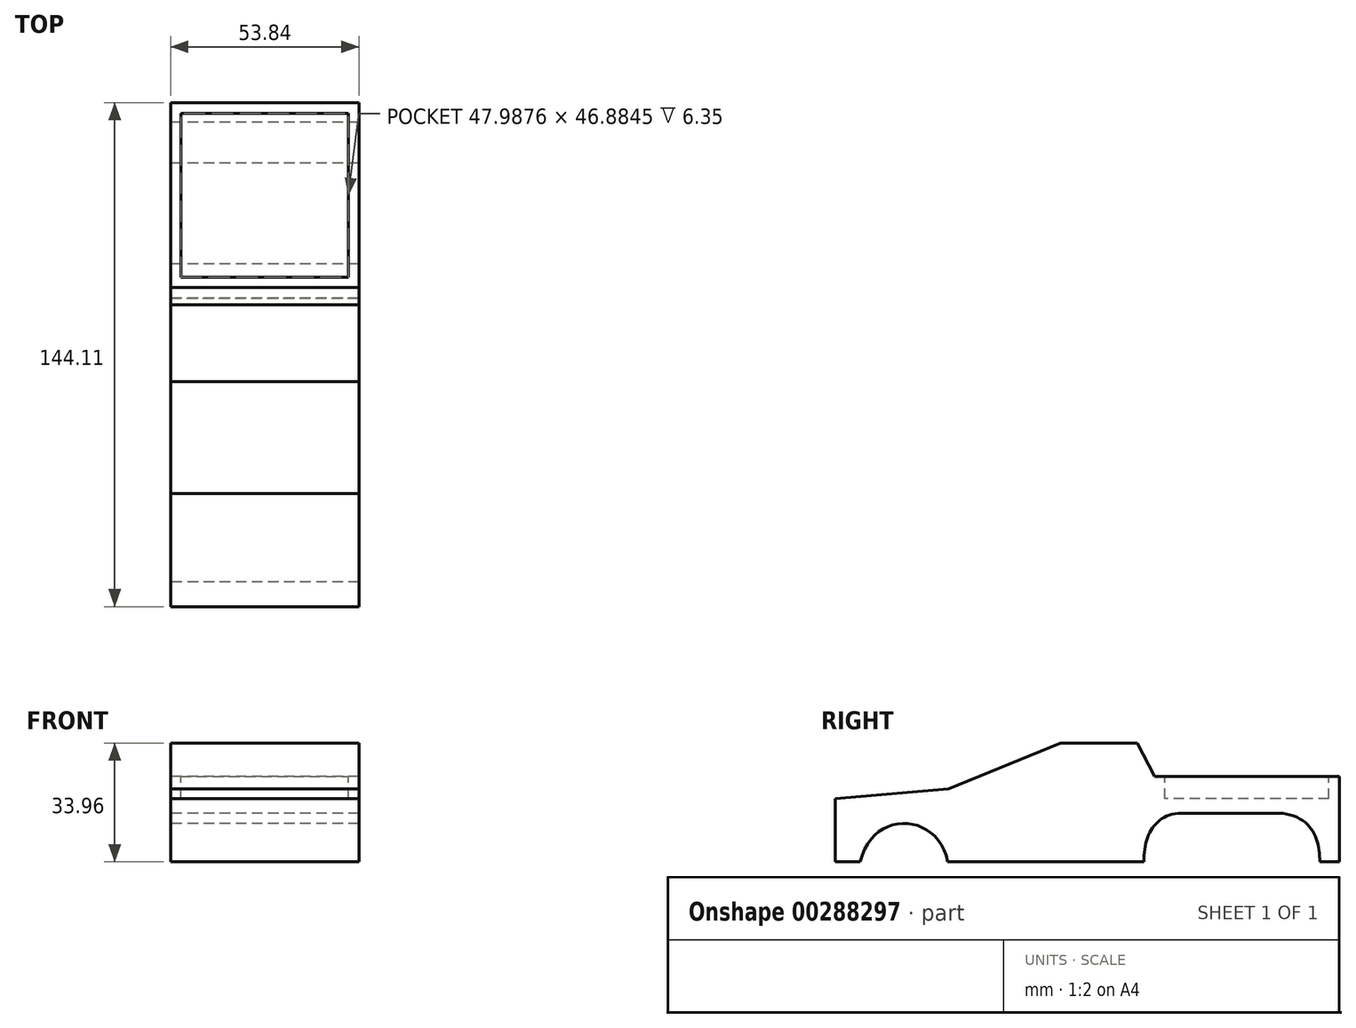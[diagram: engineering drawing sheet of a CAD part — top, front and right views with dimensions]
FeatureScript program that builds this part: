
annotation { "Feature Type Name" : "Feature", "Feature Type Description" : "" }
export const myFeature = defineFeature(function(context is Context, id is Id, definition is map)
    precondition{}
    {
        {
            var Q0;
            Q0=qCreatedBy(makeId("Right.planeOp"),FACE);
            var sketch = newSketch(context, id + "F0", { "sketchPlane" : qUnion([Q0])});
            skLineSegment(sketch, "E0", {"start": v(-64.3, -8.5) * mm, "end": v(-64.3, 9.55) * mm});
            skLineSegment(sketch, "E1", {"start": v(-64.3, 9.55) * mm, "end": v(-32.02, 12.36) * mm});
            skLineSegment(sketch, "E2", {"start": v(-32.02, 12.36) * mm, "end": v(0, 25.46) * mm});
            skLineSegment(sketch, "E3", {"start": v(0, 25.46) * mm, "end": v(22.03, 25.46) * mm});
            skLineSegment(sketch, "E4", {"start": v(22.03, 25.46) * mm, "end": v(26.94, 15.87) * mm});
            skLineSegment(sketch, "E5", {"start": v(26.94, 15.87) * mm, "end": v(79.81, 15.87) * mm});
            skLineSegment(sketch, "E6", {"start": v(79.81, 15.87) * mm, "end": v(79.81, -8.5) * mm});
            skLineSegment(sketch, "E7", {"start": v(-64.3, -8.5) * mm, "end": v(79.81, -8.5) * mm});
            skFitSpline(sketch, "E8", {"points": [v(-57.23, -8.5) * mm, v(-32.2, -8.5) * mm], "startDerivative": vector(11.04, 45.54) * mm, "endDerivative": vector(8.41, -42.38) * mm});
            skLineSegment(sketch, "E9", {"start": v(62.47, 5.42) * mm, "end": v(33.69, 5.42) * mm});
            skFitSpline(sketch, "E10", {"points": [v(62.47, 5.42) * mm, v(74.17, -8.5) * mm], "startDerivative": vector(28.57, -1.83) * mm, "endDerivative": vector(-0.15, -18.9) * mm});
            skFitSpline(sketch, "E11", {"points": [v(33.69, 5.42) * mm, v(23.92, -8.5) * mm], "startDerivative": vector(-20.9, -2.53) * mm, "endDerivative": vector(0.7, -21.7) * mm});
            skSolve(sketch);
        }
        {
            var Q0;
            {var subQ3=sQuery(id+"F0.wireOp",EDGE,"E0");Q0=makeQuery(id+"F0.imprint","IMPRINT",FACE,{"disambiguationData":[TD([[makeQuery(id+"F0.imprint","IMPRINT",EDGE,{"derivedFrom":subQ3}),-1.0]])]});}
            extrude(context, id + "F1", {"entities" : qUnion([Q0]), "endBound" : BoundingType.SYMMETRIC, "depth" : 53.85 * mm});
        }
        {
            var Q0;
            Q0=makeQuery(id+"F1.opExtrude","SWEPT_FACE",FACE,{"disambiguationData":[OSD([sQuery(id+"F0.wireOp",EDGE,"E5")])]});
            var sketch = newSketch(context, id + "F2", { "sketchPlane" : qUnion([Q0])});
            skLineSegment(sketch, "E12.bottom", {"start": v(-24.03, 76.77) * mm, "end": v(23.96, 76.77) * mm});
            skLineSegment(sketch, "E12.top", {"start": v(-24.03, 29.89) * mm, "end": v(23.96, 29.89) * mm});
            skLineSegment(sketch, "E12.left", {"start": v(-24.03, 76.77) * mm, "end": v(-24.03, 29.89) * mm});
            skLineSegment(sketch, "E12.right", {"start": v(23.96, 76.77) * mm, "end": v(23.96, 29.89) * mm});
            skSolve(sketch);
        }
        {
            var Q0;
            Q0=makeQuery(id+"F2.imprint","IMPRINT",FACE,{"disambiguationData":[TD([[makeQuery(id+"F2.imprint","IMPRINT",EDGE,{"derivedFrom":sQuery(id+"F2.wireOp",EDGE,"E12.bottom")}),-1.0]])]});
            extrude(context, id + "F3", {"entities" : qUnion([Q0]), "operationType" : NewBodyOperationType.REMOVE, "oppositeDirection" : true, "depth" : 6.35 * mm});
        }
    });
